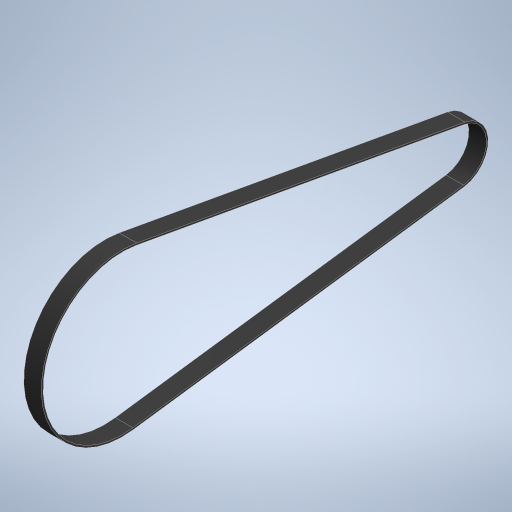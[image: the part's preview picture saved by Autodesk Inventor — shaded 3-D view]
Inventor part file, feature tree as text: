
AUTODESK INVENTOR PART (.ipt)
format: ipt  version: 2023 (Build 270158000, 158)  size: 250,368 bytes
history: native  units: mm
features: other x1, extrude x1, sketch x1
ambient origin geometry x8: Origin, YZ Plane, XZ Plane, XY Plane, X Axis, Y Axis, Z Axis, Center Point
bodies: Body1 (feature_tree)
feature tree (3):
  other  "ソリッド1"
  extrude  "押し出し1"  Depth=92.0mm
  sketch  "スケッチ1"
